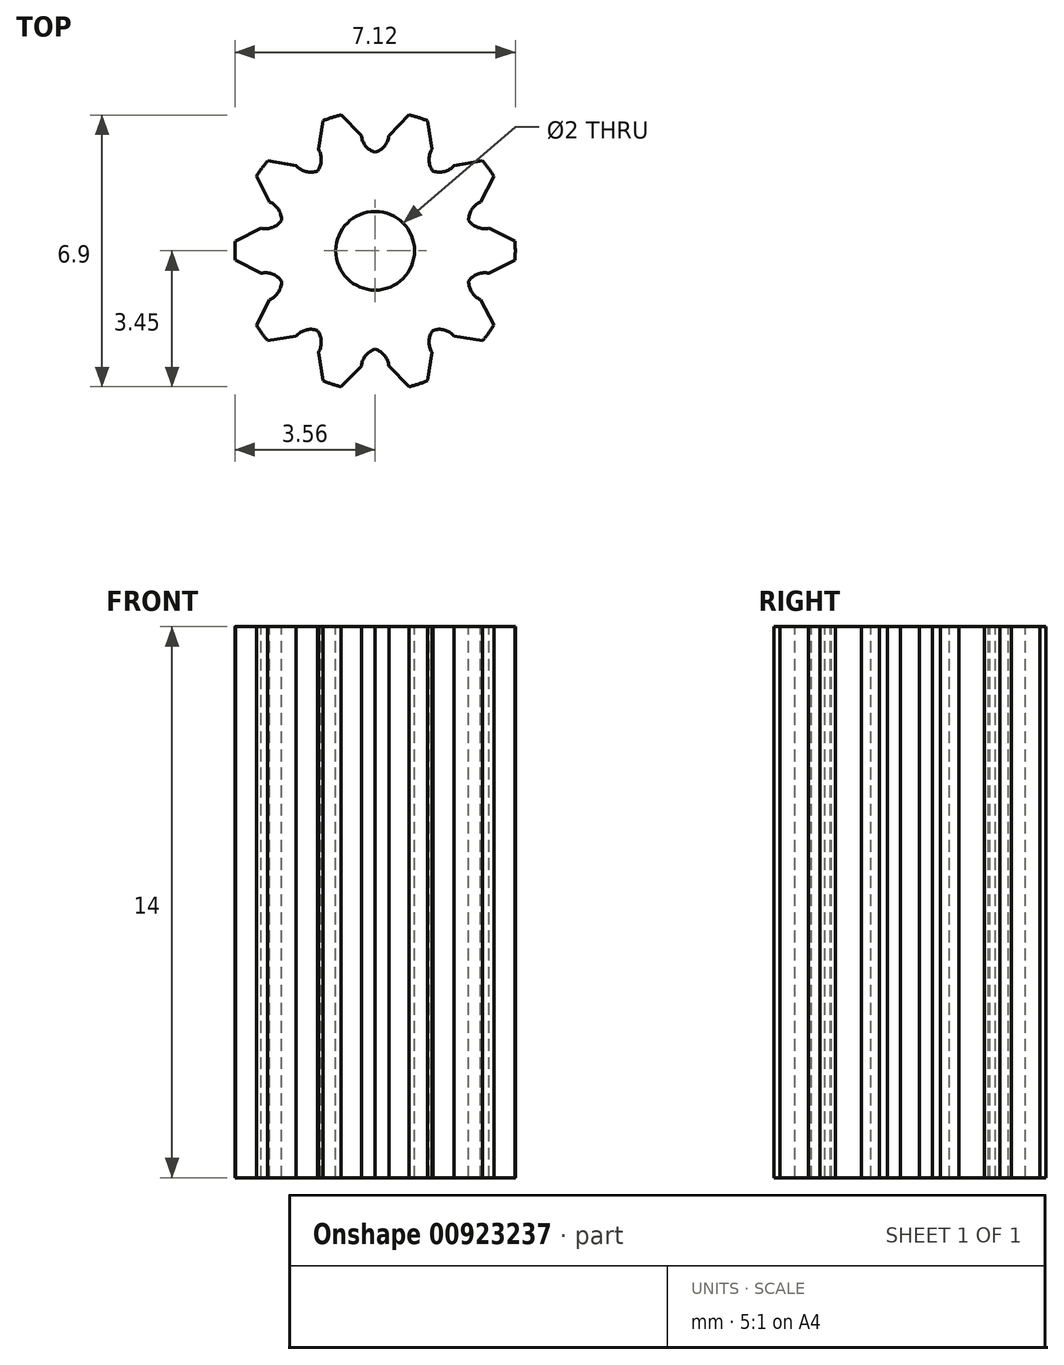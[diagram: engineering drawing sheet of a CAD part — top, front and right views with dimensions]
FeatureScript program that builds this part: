
annotation { "Feature Type Name" : "Feature", "Feature Type Description" : "" }
export const myFeature = defineFeature(function(context is Context, id is Id, definition is map)
    precondition{}
    {
        {
            var Q0;
            Q0=qCreatedBy(makeId("Top.planeOp"),FACE);
            var sketch = newSketch(context, id + "F0", { "sketchPlane" : qUnion([Q0])});
            skCircle(sketch, "E0", {"center": v(0, 0) * mm, "radius": 3.56 * mm});
            skSolve(sketch);
        }
        {
            var Q0;
            Q0 = qSketchRegion(id + "F0", true);
            extrude(context, id + "F1", {"entities" : qUnion([Q0]), "depth" : 14 * mm, "offsetDistance" : 25 * mm});
        }
        {
            var Q0;
            Q0=makeQuery(id+"F1.opExtrude","CAP_FACE",FACE,{"disambiguationData":[OSD([sQuery(id+"F0.wireOp",EDGE,"E0")])],"isStart":false});
            var sketch = newSketch(context, id + "F2", { "sketchPlane" : qUnion([Q0])});
            skCircle(sketch, "E1", {"center": v(0, 0) * mm, "radius": 1 * mm});
            skSolve(sketch);
        }
        {
            var Q0;
            Q0 = qSketchRegion(id + "F2", true);
            extrude(context, id + "F3", {"entities" : qUnion([Q0]), "operationType" : NewBodyOperationType.REMOVE, "oppositeDirection" : true, "depth" : 20.5 * mm, "offsetDistance" : 25 * mm});
        }
        {
            var Q0;
            Q0=makeQuery(id+"F1.opExtrude","CAP_FACE",FACE,{"disambiguationData":[OSD([sQuery(id+"F0.wireOp",EDGE,"E0")])],"isStart":false});
            var sketch = newSketch(context, id + "F4", { "sketchPlane" : qUnion([Q0])});
            skCircle(sketch, "E2", {"center": v(0, 0) * mm, "radius": 2.5 * mm});
            skArc(sketch, "E3", {"start": v(-0.35, 2.93) * mm, "mid": v(-0.24, 2.66) * mm, "end": v(0, 2.5) * mm});
            skLineSegment(sketch, "E4", {"start": v(-0.35, 2.93) * mm, "end": v(-0.87, 3.45) * mm});
            skArc(sketch, "E5.MirrorCS", {"start": v(0.35, 2.93) * mm, "mid": v(0.24, 2.66) * mm, "end": v(0, 2.5) * mm});
            skLineSegment(sketch, "E6.MirrorCS", {"start": v(0.35, 2.93) * mm, "end": v(0.87, 3.45) * mm});
            skSolve(sketch);
        }
        {
            var Q0;
            Q0=makeQuery(id+"F4.imprint","IMPRINT",FACE,{"disambiguationData":[TD([[makeQuery(id+"F4.imprint","IMPRINT",EDGE,{"derivedFrom":sQuery(id+"F4.wireOp",EDGE,"E3")}),1.0]])]});
            extrude(context, id + "F5", {"entities" : qUnion([Q0]), "operationType" : NewBodyOperationType.REMOVE, "oppositeDirection" : true, "depth" : 14 * mm, "offsetDistance" : 25 * mm});
        }
        {
            var Q0;
            Q0=makeQuery(id+"F5.boolean.opBoolean","COPY",FACE,{"derivedFrom":makeQuery(id+"F5.opExtrude","SWEPT_FACE",FACE,{"disambiguationData":[OSD([sQuery(id+"F4.wireOp",EDGE,"E4")])]})});
            var Q1;
            Q1=makeQuery(id+"F5.boolean.opBoolean","COPY",FACE,{"derivedFrom":makeQuery(id+"F5.opExtrude","SWEPT_FACE",FACE,{"disambiguationData":[OSD([sQuery(id+"F4.wireOp",EDGE,"E3")])]})});
            var Q2;
            Q2=makeQuery(id+"F5.boolean.opBoolean","COPY",FACE,{"derivedFrom":makeQuery(id+"F5.opExtrude","SWEPT_FACE",FACE,{"disambiguationData":[OSD([sQuery(id+"F4.wireOp",EDGE,"E5.MirrorCS")])]})});
            var Q3;
            Q3=makeQuery(id+"F5.boolean.opBoolean","COPY",FACE,{"derivedFrom":makeQuery(id+"F5.opExtrude","SWEPT_FACE",FACE,{"disambiguationData":[OSD([sQuery(id+"F4.wireOp",EDGE,"E6.MirrorCS")])]})});
            var Q4;
            Q4=makeQuery(id+"F1.opExtrude","SWEPT_FACE",FACE,{"disambiguationData":[OSD([sQuery(id+"F0.wireOp",EDGE,"E0")])]});
            circularPattern(context, id + "F6", {"patternType" : PatternType.FACE, "faces" : qUnion([Q0, Q1, Q2, Q3]), "axis" : qUnion([Q4]), "angle" : 360 * degree, "instanceCount" : 10, "equalSpace" : true});
        }
    });
